# Revit family: QF_ADVENTYS_ADV1471-C_DRIC_3600
name_source: partatom
category: Attrezzature speciali
units: mm (PartAtom-declared; Revit-internal decimal feet)

## family parameters
Condiviso = No
Host = Superficie
Punto di calcolo locali = No
Quota connettore circolare = Usa diametro
Taglio con vuoti quando caricato = No
Tipo di parte = Normale

## types (1)
- ADV1471-C
    Cycle = 50 Hz
    Depth = 580 mm  [stored 1.90289 ft]
    Depth Actual = 440 mm  [stored 1.44357 ft]
    Depth_Cooking = 407 mm  [stored 1.3353 ft]
    Depth_Cutout = 550 mm
    Depth_Generator = 515.6 mm  [stored 1.6916 ft]
    EI_X = 75 mm
    EI_Y = 45 mm  [stored 0.147638 ft]
    Height = 224.5 mm  [stored 0.736549 ft]
    Height Actual = 171 mm  [stored 0.561024 ft]
    Height_Generator = 70.1 mm  [stored 0.229987 ft]
    Item Number = ADV1471-C
    Length Actual = 580 mm  [stored 1.90289 ft]
    Modello = DRIC 3600
    Phase = 1
    Produttore = ADVENTYS
    Prospetto di default = 1219.2 mm  [stored 4 ft]
    URL = https://adventys.com
    Volts = 220 V
    Watts = 3600 W
    Weight = 9.5
    Width = 440 mm  [stored 1.44357 ft]
    Width_Cooking = 342 mm  [stored 1.12205 ft]
    Width_Cutout = 410 mm  [stored 1.34514 ft]
    Width_Generator = 378 mm  [stored 1.24016 ft]

note: [stored X ft] marks values corroborated as IEEE doubles in the binary element streams (Revit-internal decimal feet)

## geometry (parser evidence)
native form markers: Blend x4
no freeform markers — native parametric forms only
